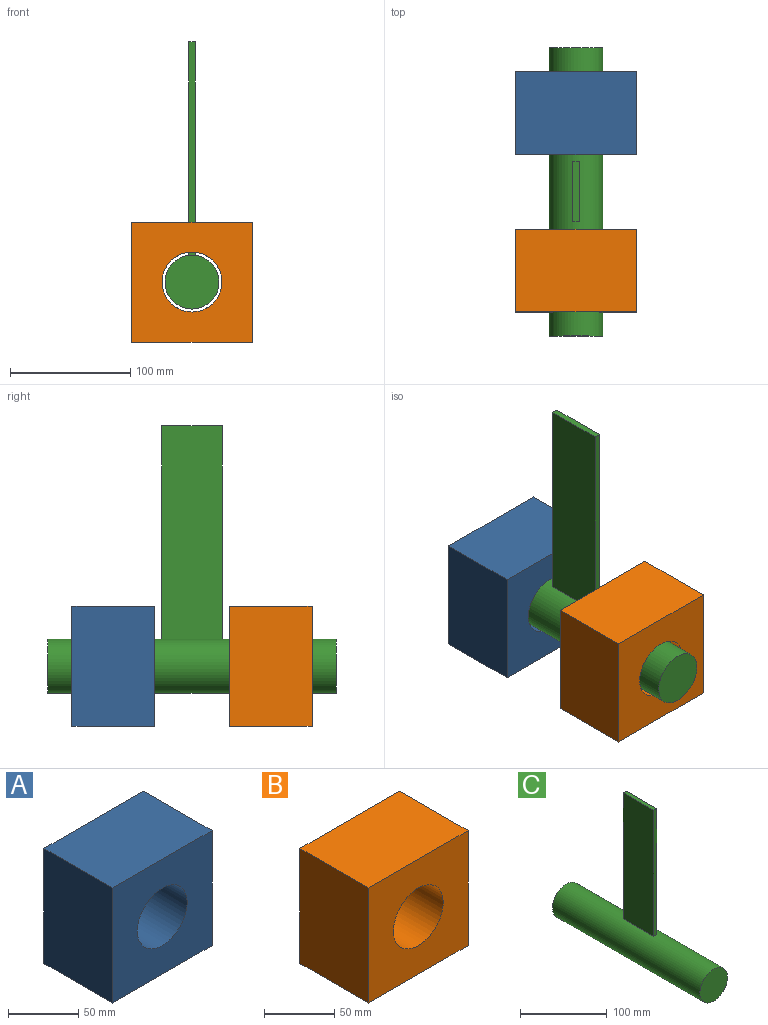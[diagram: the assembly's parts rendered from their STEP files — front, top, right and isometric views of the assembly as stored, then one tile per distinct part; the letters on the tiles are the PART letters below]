
ASSEMBLY  parts=3 mates=2
PART A: 7 faces, bbox 100x68.8x100 mm
  f0: plane 100x68.84mm, normal (0,0,1), area 6884.5mm2, adj f1,f2,f4,f5
  f1: plane 100x68.84mm, normal (1,0,0), area 6884.5mm2, adj f0,f3,f4,f5
  f2: plane 100x68.84mm, normal (-1,0,0), area 6884.5mm2, adj f0,f3,f4,f5
  f3: plane 100x68.84mm, normal (0,0,-1), area 6884.5mm2, adj f1,f2,f4,f5
  f4: plane 100x100mm, normal (0,1,0), area 8036.5mm2, adj f0,f1,f2,f3,f6
  f5: plane 100x100mm, normal (0,-1,0), area 8036.5mm2, adj f0,f1,f2,f3,f6
  f6: cylinder r=25mm len=68.84mm, axis (0,-1,0), area 10814.1mm2, adj f4,f5
PART B: 7 faces, bbox 100x68.8x100 mm
  f0: plane 100x100mm, normal (0,-1,0), area 8036.5mm2, adj f1,f2,f3,f4,f6
  f1: plane 100x68.84mm, normal (0,0,-1), area 6884.5mm2, adj f0,f2,f4,f5
  f2: plane 100x68.84mm, normal (-1,0,0), area 6884.5mm2, adj f0,f1,f3,f5
  f3: plane 100x68.84mm, normal (0,0,1), area 6884.5mm2, adj f0,f2,f4,f5
  f4: plane 100x68.84mm, normal (1,0,0), area 6884.5mm2, adj f0,f1,f3,f5
  f5: plane 100x100mm, normal (0,1,0), area 8036.5mm2, adj f1,f2,f3,f4,f6
  f6: cylinder r=25mm len=68.84mm, axis (0,-1,0), area 10814.1mm2, adj f0,f5
PART C: 8 faces, bbox 45x240x222.5 mm
  f0: cylinder r=22.5mm len=240mm, axis (0,1,0), area 33678.7mm2, adj f1,f2,f3,f4,f5,f6
  f1: plane 45x45mm, normal (0,-1,0), area 1590.4mm2, adj f0
  f2: plane 45x45mm, normal (0,1,0), area 1590.4mm2, adj f0
  f3: plane 177.64x50mm, normal (1,0,0), area 8882mm2, adj f0,f5,f6,f7
  f4: plane 177.64x50mm, normal (-1,0,0), area 8882mm2, adj f0,f5,f6,f7
  f5: plane 177.64x5mm, normal (0,1,0), area 887.7mm2, adj f0,f3,f4,f7
  f6: plane 177.64x5mm, normal (0,-1,0), area 887.7mm2, adj f0,f3,f4,f7
  f7: plane 50x5mm, normal (0,0,1), area 250mm2, adj f3,f4,f5,f6
PLACE A t=(0,65.58,50)mm
PLACE B t=(0,65.58,50)mm
PLACE C rot(axis=(0.06,1,0),0deg) t=(0,65.58,50)mm
MATE revolute B.f6 <-> C.f0  axis (0,-1,0) through (0,-34.42,50)mm
MATE fastened A.f6 <-> B.f6  axis (0,1,0) through (0,165.58,50)mm
